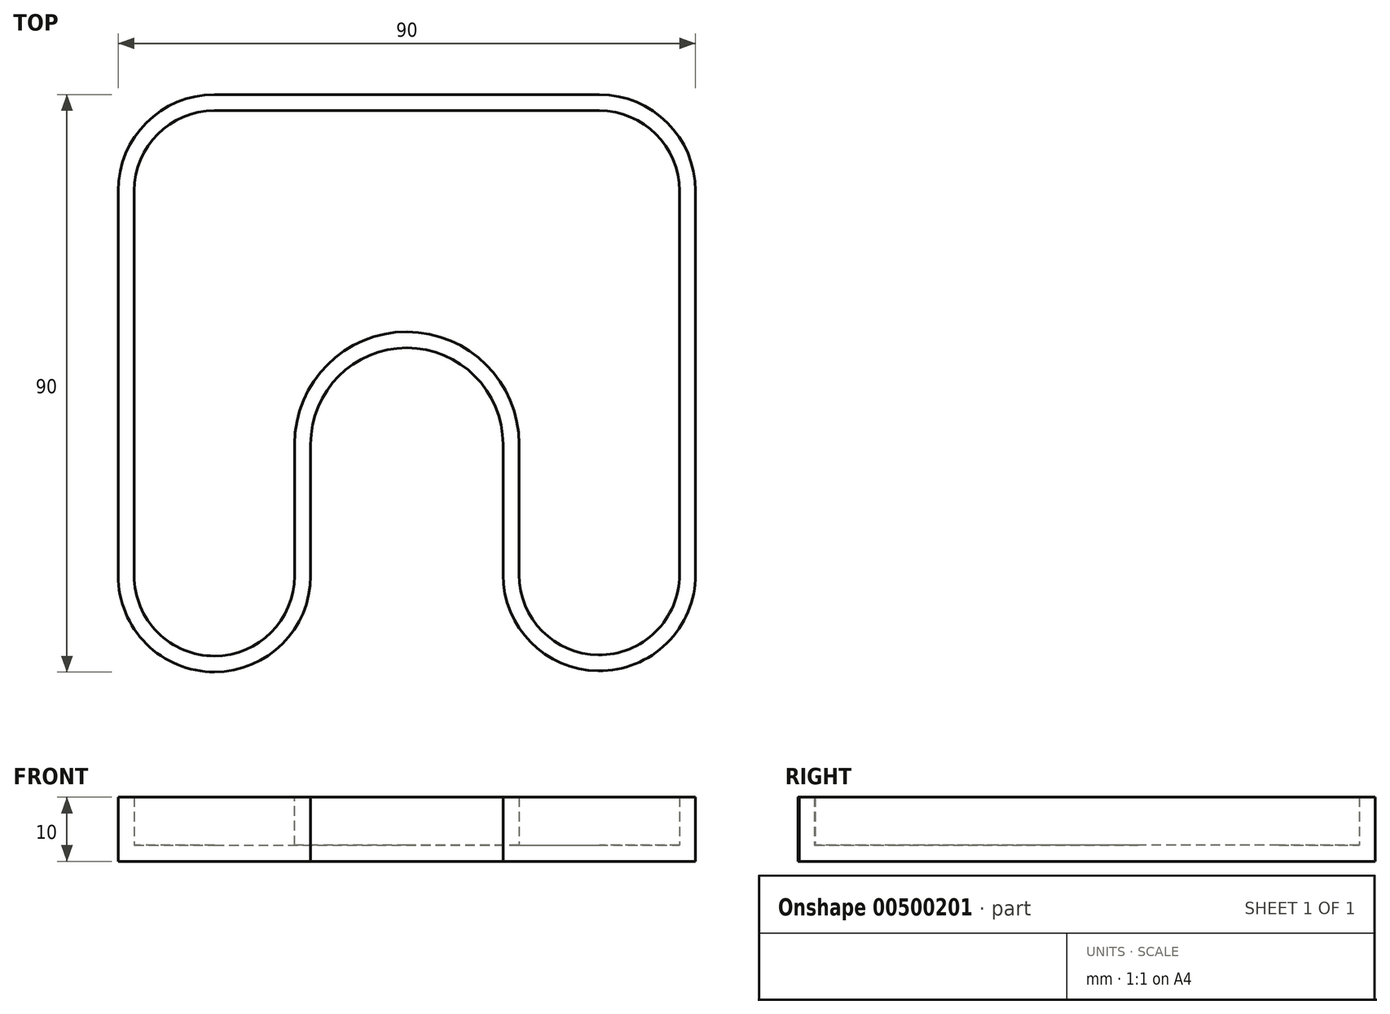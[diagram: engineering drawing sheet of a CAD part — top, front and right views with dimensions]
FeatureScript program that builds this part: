
annotation { "Feature Type Name" : "Feature", "Feature Type Description" : "" }
export const myFeature = defineFeature(function(context is Context, id is Id, definition is map)
    precondition{}
    {
        {
            var Q0;
            Q0=qCreatedBy(makeId("Top.planeOp"),FACE);
            var sketch = newSketch(context, id + "F0", { "sketchPlane" : qUnion([Q0])});
            skLineSegment(sketch, "E0.bottom", {"start": v(-34.22, 39.48) * mm, "end": v(25.78, 39.48) * mm});
            skLineSegment(sketch, "E0.left", {"start": v(-49.22, 24.48) * mm, "end": v(-49.22, -35.52) * mm});
            skLineSegment(sketch, "E0.right", {"start": v(40.78, 24.48) * mm, "end": v(40.78, -35.35) * mm});
            skLineSegment(sketch, "E1", {"start": v(-19.22, -35.52) * mm, "end": v(-19.22, -15) * mm});
            skLineSegment(sketch, "E2", {"start": v(10.78, -15) * mm, "end": v(10.78, -35.35) * mm});
            skLineSegment(sketch, "E3", {"start": v(-34.22, -50.52) * mm, "end": v(-34.22, -50.52) * mm});
            skLineSegment(sketch, "E4", {"start": v(25.6, -50.35) * mm, "end": v(25.6, -50.35) * mm});
            skLineSegment(sketch, "E5", {"start": v(-4.22, 0) * mm, "end": v(-4.22, 0) * mm});
            skPoint(sketch, "E6.visualSharp", {"position": v(-19.22, 0) * mm});
            skArc(sketch, "E6.filletArc", {"start": v(-4.22, 0) * mm, "mid": v(-14.83, -4.4) * mm, "end": v(-19.22, -15) * mm});
            skPoint(sketch, "E7.newPointA", {"position": v(10.78, 1.12) * mm});
            skPoint(sketch, "E7.newPointB", {"position": v(10.78, 0) * mm});
            skArc(sketch, "E7.filletArc", {"start": v(10.78, -15) * mm, "mid": v(6.38, -4.4) * mm, "end": v(-4.22, 0) * mm});
            skPoint(sketch, "E8.visualSharp", {"position": v(10.78, -50.18) * mm});
            skArc(sketch, "E8.filletArc", {"start": v(10.78, -35.35) * mm, "mid": v(15.11, -45.9) * mm, "end": v(25.6, -50.35) * mm});
            skPoint(sketch, "E9.visualSharp", {"position": v(40.78, -50.52) * mm});
            skArc(sketch, "E9.filletArc", {"start": v(25.6, -50.35) * mm, "mid": v(36.32, -46.02) * mm, "end": v(40.78, -35.35) * mm});
            skPoint(sketch, "E10.visualSharp", {"position": v(40.78, 39.48) * mm});
            skArc(sketch, "E10.filletArc", {"start": v(40.78, 24.48) * mm, "mid": v(36.38, 35.08) * mm, "end": v(25.78, 39.48) * mm});
            skPoint(sketch, "E11.visualSharp", {"position": v(-49.22, 39.48) * mm});
            skArc(sketch, "E11.filletArc", {"start": v(-34.22, 39.48) * mm, "mid": v(-44.83, 35.08) * mm, "end": v(-49.22, 24.48) * mm});
            skPoint(sketch, "E12.visualSharp", {"position": v(-49.22, -50.52) * mm});
            skArc(sketch, "E12.filletArc", {"start": v(-49.22, -35.52) * mm, "mid": v(-44.83, -46.13) * mm, "end": v(-34.22, -50.52) * mm});
            skPoint(sketch, "E13.visualSharp", {"position": v(-19.22, -50.52) * mm});
            skArc(sketch, "E13.filletArc", {"start": v(-34.22, -50.52) * mm, "mid": v(-23.62, -46.13) * mm, "end": v(-19.22, -35.52) * mm});
            skSolve(sketch);
        }
        {
            var Q0;
            Q0 = qSketchRegion(id + "F0", true);
            extrude(context, id + "F1", {"entities" : qUnion([Q0]), "depth" : 10 * mm});
        }
        {
            var Q0;
            Q0=makeQuery(id+"F1.opExtrude","CAP_FACE",FACE,{"disambiguationData":[OSD([sQuery(id+"F0.wireOp",EDGE,"E0.bottom"),sQuery(id+"F0.wireOp",EDGE,"E0.left"),sQuery(id+"F0.wireOp",EDGE,"E0.right"),sQuery(id+"F0.wireOp",EDGE,"E1"),sQuery(id+"F0.wireOp",EDGE,"E2"),sQuery(id+"F0.wireOp",EDGE,"E3"),sQuery(id+"F0.wireOp",EDGE,"E5"),sQuery(id+"F0.wireOp",EDGE,"E6.filletArc"),sQuery(id+"F0.wireOp",EDGE,"E7.filletArc"),sQuery(id+"F0.wireOp",EDGE,"E8.filletArc"),sQuery(id+"F0.wireOp",EDGE,"E9.filletArc"),sQuery(id+"F0.wireOp",EDGE,"E10.filletArc"),sQuery(id+"F0.wireOp",EDGE,"E11.filletArc"),sQuery(id+"F0.wireOp",EDGE,"E12.filletArc"),sQuery(id+"F0.wireOp",EDGE,"E13.filletArc")])],"isStart":false});
            shell(context, id + "F2", {"entities" : qUnion([Q0]), "thickness" : 2.5 * mm});
        }
    });
